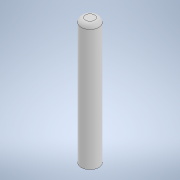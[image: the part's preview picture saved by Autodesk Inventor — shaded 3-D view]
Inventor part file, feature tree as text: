
AUTODESK INVENTOR PART (.ipt)
format: ipt  version: 2022 (Build 260153000, 153)  size: 99,840 bytes
history: native  units: mm
features: extrude x1, fillet x1, sketch x1
ambient origin geometry x8: Origin, YZ Plane, XZ Plane, XY Plane, X Axis, Y Axis, Z Axis, Center Point
bodies: Solid1 (feature_tree)
feature tree (3):
  extrude  "Extrusion1"  Depth=15.0mm TaperAngle=0.0deg
  fillet  "Fillet1"  Radius=0.5mm
  sketch  "Sketch1"  dims[d0=2.1mm d1=15.0mm d2=0.0mm d3=0.5mm]
